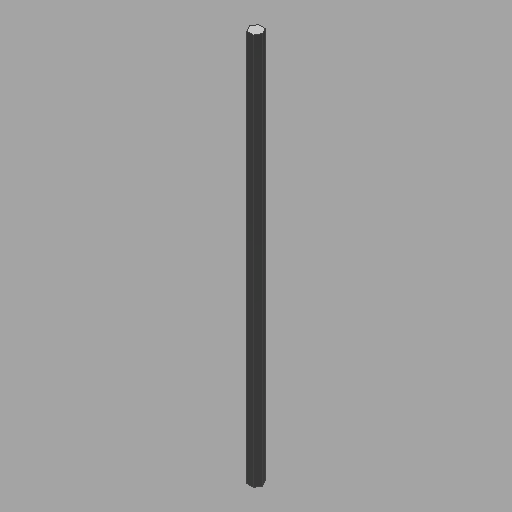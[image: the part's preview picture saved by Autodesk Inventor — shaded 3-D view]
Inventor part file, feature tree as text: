
AUTODESK INVENTOR PART (.ipt)
format: ipt  version: 2024.2 (Build 282272000, 272)  size: 454,656 bytes
history: native  units: in
note: dims shown in document units (in); Inventor stores cm internally (conversion verified against a paired STEP export)
features: extrude x32, other x4, hole x2
ambient origin geometry x8: Origin, YZ Plane, XZ Plane, XY Plane, X Axis, Y Axis, Z Axis, Center Point
bodies: Solid3 (feature_tree)
feature tree (38):
  extrude  "BaseProfile625Round"  Depth=0.5in
  extrude  "BaseProfileRoundTube"  Depth=0.5413in
  extrude  "BaseProfile500Hex"  Depth=0.5in
  extrude  "BaseProfile500Thunderhex"  Depth=0.375in
  extrude  "BaseProfile500Round"  Depth=0.4035in
  extrude  "BaseProfile375Hex"  Depth=0.75in
  extrude  "BaseProfile375Thunderhex"  Depth=0.468in
  extrude  "BaseProfile375Round"  Depth=0.201in
  extrude  "TopShaftProfile1Hex500"  Depth=0.159in
  extrude  "TopShaftProfile1ThunderHex500"  Depth=0.25in
  extrude  "TopShaftProfile1Round500"  Depth=36.0in TaperAngle=0.0deg
  extrude  "TopShaftProfile1Hex375"  Depth=17.0in TaperAngle=0.0deg
  extrude  "TopShaftProfile1ThunderHex375"  Depth=36.0in TaperAngle=0.0deg
  extrude  "TopShaftProfile1Round375"  Depth=36.0in TaperAngle=0.0deg
  extrude  "TopShaftProfile2ThunderHex500"  Depth=36.0in TaperAngle=0.0deg
  extrude  "TopShaftProfile2Round500"  Depth=36.0in TaperAngle=0.0deg
  extrude  "TopShaftProfile2Hex375"  Depth=36.0in TaperAngle=0.0deg
  extrude  "TopShaftProfile2ThunderHex375"  Depth=36.0in TaperAngle=0.0deg
  extrude  "TopShaftProfile2Round375"  Depth=36.0in TaperAngle=0.0deg
  other  "TopRetentionGroove&BearingRound"
  hole  "TopShaftTappedHole"  [1 undecoded]
  other  "TopShaftThread"
  extrude  "BottomShaftProfile1Hex500"  TaperAngle=0.0deg  [1 undecoded]
  extrude  "BottomShaftProfile1ThunderHex500"  TaperAngle=0.0deg  [1 undecoded]
  extrude  "BottomShaftProfile1Round500"  TaperAngle=0.0deg  [1 undecoded]
  extrude  "BottomShaftProfile1Hex375"  TaperAngle=0.0deg  [1 undecoded]
  extrude  "BottomShaftProfile1ThunderHex375"  TaperAngle=0.0deg  [1 undecoded]
  extrude  "BottomShaftProfile2ThunderHex500"  TaperAngle=0.0deg  [1 undecoded]
  extrude  "BottomShaftProfile1Round375"  TaperAngle=0.0deg  [1 undecoded]
  extrude  "BottomShaftProfile2Round500"  TaperAngle=0.0deg  [1 undecoded]
  extrude  "BottomShaftProfile2Hex375"  TaperAngle=0.0deg  [1 undecoded]
  extrude  "BottomShaftProfile2ThunderHex375"  TaperAngle=0.0deg  [1 undecoded]
  extrude  "BottomShaftProfile2Round375"  TaperAngle=0.0deg  [1 undecoded]
  hole  "BottomShaftTappedHole"  [1 undecoded]
  other  "BottomShaftThread"
  other  "BottomRetentionGroove&BearingRound"
  extrude  "BaseProfile375ThunderhexHole"  TaperAngle=0.0deg  [1 undecoded]
  extrude  "BaseProfile500ThunderhexHole"  TaperAngle=0.0deg  [1 undecoded]
note: 15 required parameter values undecoded (feature->parameter linkage not recoverable at this tier; creation-order binding heuristic only, values carry confidence <= 0.55)
